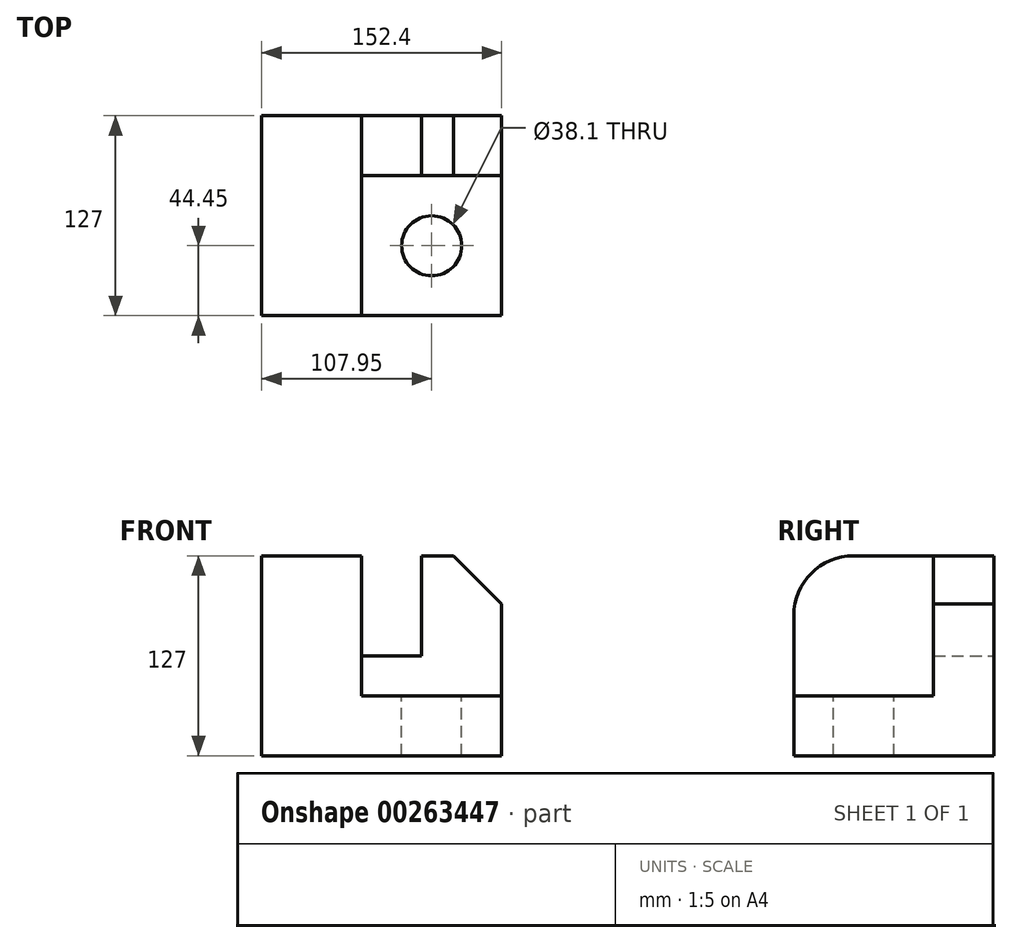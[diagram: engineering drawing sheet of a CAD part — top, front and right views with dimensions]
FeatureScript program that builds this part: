
annotation { "Feature Type Name" : "Feature", "Feature Type Description" : "" }
export const myFeature = defineFeature(function(context is Context, id is Id, definition is map)
    precondition{}
    {
        {
            var Q0;
            Q0=qCreatedBy(makeId("Front.planeOp"),FACE);
            var sketch = newSketch(context, id + "F0", { "sketchPlane" : qUnion([Q0])});
            skLineSegment(sketch, "E0.bottom", {"start": v(-76.2, 63.5) * mm, "end": v(76.2, 63.5) * mm});
            skLineSegment(sketch, "E0.top", {"start": v(-76.2, -63.5) * mm, "end": v(76.2, -63.5) * mm});
            skLineSegment(sketch, "E0.left", {"start": v(-76.2, 63.5) * mm, "end": v(-76.2, -63.5) * mm});
            skLineSegment(sketch, "E0.right", {"start": v(76.2, 63.5) * mm, "end": v(76.2, -63.5) * mm});
            skPoint(sketch, "E0.middle", {"position": v(0, 0) * mm});
            skSolve(sketch);
        }
        {
            var Q0;
            Q0=makeQuery(id+"F0.imprint","IMPRINT",FACE,{"disambiguationData":[TD([[makeQuery(id+"F0.imprint","IMPRINT",EDGE,{"derivedFrom":sQuery(id+"F0.wireOp",EDGE,"E0.bottom")}),-1.0]])]});
            extrude(context, id + "F1", {"entities" : qUnion([Q0]), "depth" : 127 * mm});
        }
        {
            var Q0;
            Q0=makeQuery(id+"F1.opExtrude","SWEPT_FACE",FACE,{"disambiguationData":[OSD([sQuery(id+"F0.wireOp",EDGE,"E0.bottom")])]});
            var sketch = newSketch(context, id + "F2", { "sketchPlane" : qUnion([Q0])});
            skLineSegment(sketch, "E1.bottom", {"start": v(76.2, -127) * mm, "end": v(-12.7, -127) * mm});
            skLineSegment(sketch, "E1.top", {"start": v(76.2, -38.1) * mm, "end": v(-12.7, -38.1) * mm});
            skLineSegment(sketch, "E1.left", {"start": v(76.2, -127) * mm, "end": v(76.2, -38.1) * mm});
            skLineSegment(sketch, "E1.right", {"start": v(-12.7, -127) * mm, "end": v(-12.7, -38.1) * mm});
            skSolve(sketch);
        }
        {
            var Q0;
            Q0=makeQuery(id+"F2.imprint","IMPRINT",FACE,{"disambiguationData":[TD([[makeQuery(id+"F2.imprint","IMPRINT",EDGE,{"derivedFrom":sQuery(id+"F2.wireOp",EDGE,"E1.bottom")}),1.0]])]});
            extrude(context, id + "F3", {"entities" : qUnion([Q0]), "operationType" : NewBodyOperationType.REMOVE, "oppositeDirection" : true, "depth" : 88.9 * mm});
        }
        {
            var Q0;
            Q0=makeQuery(id+"F3.boolean.opBoolean","COPY",FACE,{"derivedFrom":makeQuery(id+"F3.opExtrude","CAP_FACE",FACE,{"disambiguationData":[OSD([sQuery(id+"F2.wireOp",EDGE,"E1.bottom"),sQuery(id+"F2.wireOp",EDGE,"E1.top"),sQuery(id+"F2.wireOp",EDGE,"E1.left"),sQuery(id+"F2.wireOp",EDGE,"E1.right")])],"isStart":false})});
            var sketch = newSketch(context, id + "F4", { "sketchPlane" : qUnion([Q0])});
            skCircle(sketch, "E2", {"center": v(31.75, -82.55) * mm, "radius": 19.05 * mm});
            skSolve(sketch);
        }
        {
            var Q0;
            Q0=makeQuery(id+"F4.imprint","IMPRINT",FACE,{"disambiguationData":[TD([[makeQuery(id+"F4.imprint","IMPRINT",EDGE,{"derivedFrom":sQuery(id+"F4.wireOp",EDGE,"E2")}),1.0]])]});
            extrude(context, id + "F5", {"entities" : qUnion([Q0]), "operationType" : NewBodyOperationType.REMOVE, "oppositeDirection" : true, "depth" : 50.8 * mm});
        }
        {
            var Q0;
            Q0=makeQuery(id+"F1.opExtrude","SWEPT_FACE",FACE,{"disambiguationData":[OSD([sQuery(id+"F0.wireOp",EDGE,"E0.bottom")])]});
            var sketch = newSketch(context, id + "F6", { "sketchPlane" : qUnion([Q0])});
            skLineSegment(sketch, "E3.bottom", {"start": v(-12.7, -38.1) * mm, "end": v(25.4, -38.1) * mm});
            skLineSegment(sketch, "E3.top", {"start": v(-12.7, 0) * mm, "end": v(25.4, 0) * mm});
            skLineSegment(sketch, "E3.left", {"start": v(-12.7, -38.1) * mm, "end": v(-12.7, 0) * mm});
            skLineSegment(sketch, "E3.right", {"start": v(25.4, -38.1) * mm, "end": v(25.4, 0) * mm});
            skSolve(sketch);
        }
        {
            var Q0;
            Q0=makeQuery(id+"F6.imprint","IMPRINT",FACE,{"disambiguationData":[TD([[makeQuery(id+"F6.imprint","IMPRINT",EDGE,{"derivedFrom":sQuery(id+"F6.wireOp",EDGE,"E3.bottom")}),-1.0]])]});
            extrude(context, id + "F7", {"entities" : qUnion([Q0]), "operationType" : NewBodyOperationType.REMOVE, "oppositeDirection" : true, "depth" : 63.5 * mm});
        }
        {
            var Q0;
            Q0=makeQuery(id+"F1.opExtrude","SWEPT_EDGE",EDGE,{"disambiguationData":[OSD([sQuery(id+"F0.wireOp",EDGE,"E0.bottom"),sQuery(id+"F0.wireOp",EDGE,"E0.right")])]});
            chamfer(context, id + "F8", {"entities" : qUnion([Q0]), "width" : 30.48 * mm, "tangentPropagation" : true});
        }
        {
            var Q0;
            Q0=makeQuery(id+"F1.opExtrude","CAP_EDGE",EDGE,{"disambiguationData":[OSD([sQuery(id+"F0.wireOp",EDGE,"E0.bottom")])],"isStart":false});
            fillet(context, id + "F9", {"entities" : qUnion([Q0]), "radius" : 38.1 * mm, "tangentPropagation" : true, "allowEdgeOverflow" : false});
        }
    });
